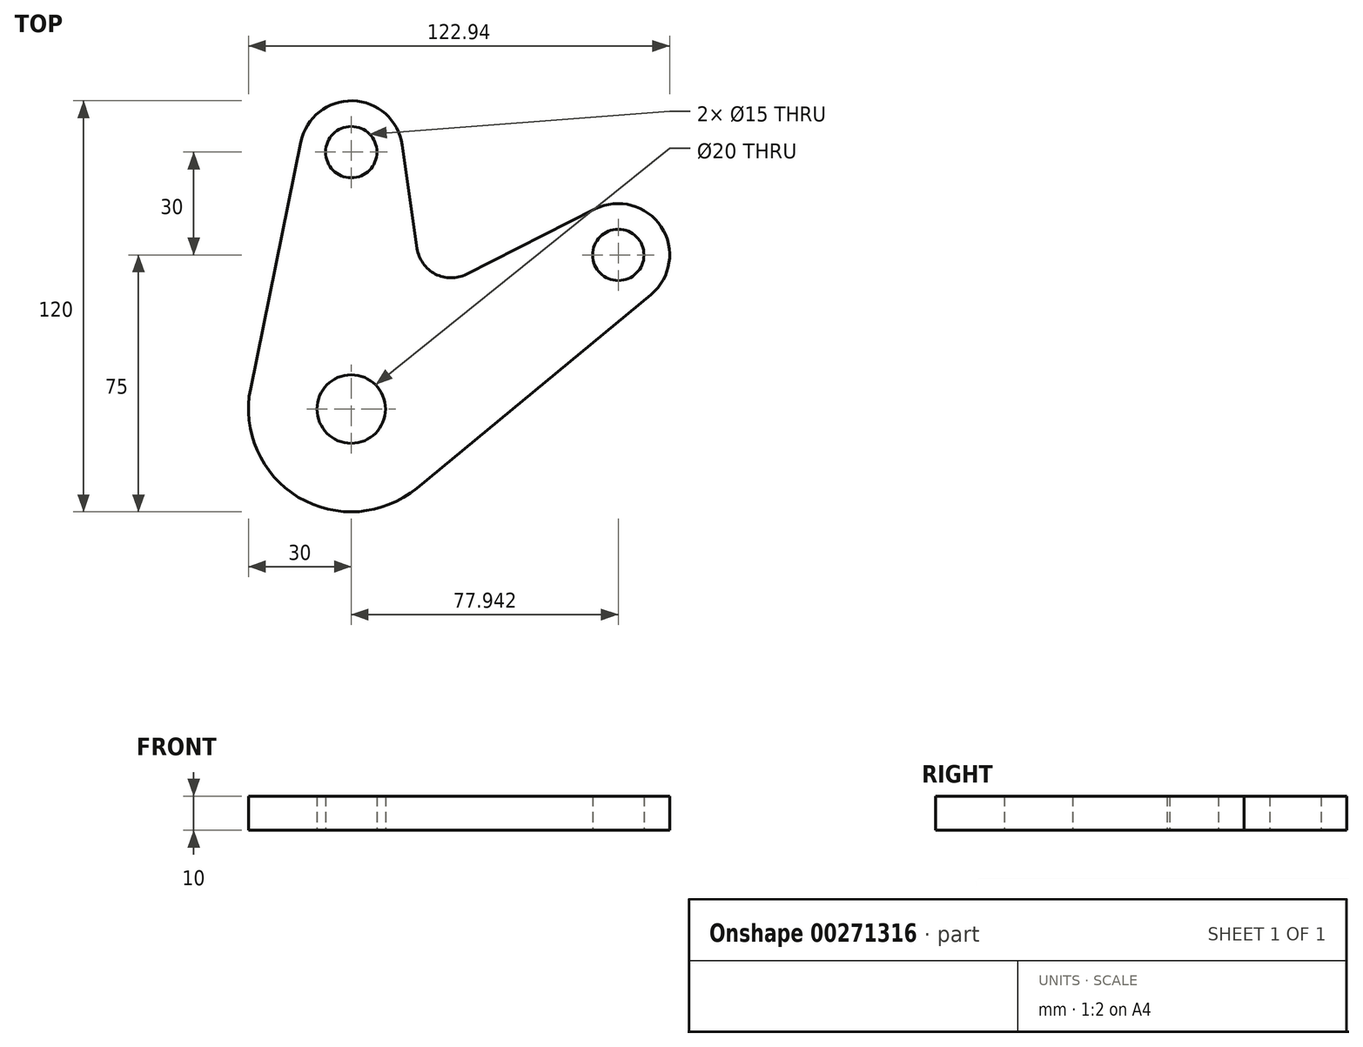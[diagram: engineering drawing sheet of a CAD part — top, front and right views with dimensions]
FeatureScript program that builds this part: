
annotation { "Feature Type Name" : "Feature", "Feature Type Description" : "" }
export const myFeature = defineFeature(function(context is Context, id is Id, definition is map)
    precondition{}
    {
        {
            var Q0;
            Q0=qCreatedBy(makeId("Top.planeOp"),FACE);
            var sketch = newSketch(context, id + "F0", { "sketchPlane" : qUnion([Q0])});
            skPoint(sketch, "E0", {"position": v(0, 0) * mm});
            skCircle(sketch, "E1", {"center": v(0, 0) * mm, "radius": 10 * mm});
            skArc(sketch, "E2", {"start": v(-29.4, 6) * mm, "mid": v(-15.44, -25.72) * mm, "end": v(19.12, -23.12) * mm});
            skCircle(sketch, "E3", {"center": v(77.94, 45) * mm, "radius": 7.5 * mm});
            skArc(sketch, "E4", {"start": v(87.5, 33.44) * mm, "mid": v(90.49, 53.22) * mm, "end": v(71.16, 58.38) * mm});
            skCircle(sketch, "E5", {"center": v(0, 75) * mm, "radius": 7.5 * mm});
            skArc(sketch, "E6", {"start": v(14.84, 77.15) * mm, "mid": v(0.43, 90) * mm, "end": v(-14.7, 78) * mm});
            skLineSegment(sketch, "E7", {"start": v(-14.7, 78) * mm, "end": v(-29.4, 6) * mm});
            skLineSegment(sketch, "E8", {"start": v(19.12, -23.12) * mm, "end": v(87.5, 33.44) * mm});
            skLineSegment(sketch, "E9", {"start": v(71.16, 58.38) * mm, "end": v(33.65, 39.38) * mm});
            skLineSegment(sketch, "E10", {"start": v(14.84, 77.15) * mm, "end": v(19.23, 46.86) * mm});
            skPoint(sketch, "E11.visualSharp", {"position": v(21.23, 33.09) * mm});
            skArc(sketch, "E11.filletArc", {"start": v(19.23, 46.86) * mm, "mid": v(24.52, 39.42) * mm, "end": v(33.65, 39.38) * mm});
            skSolve(sketch);
        }
        {
            var Q0;
            Q0=makeQuery(id+"F0.imprint","IMPRINT",FACE,{"disambiguationData":[TD([[makeQuery(id+"F0.imprint","IMPRINT",EDGE,{"derivedFrom":sQuery(id+"F0.wireOp",EDGE,"E1")}),-1.0]])]});
            extrude(context, id + "F1", {"entities" : qUnion([Q0]), "depth" : 10 * mm});
        }
    });
